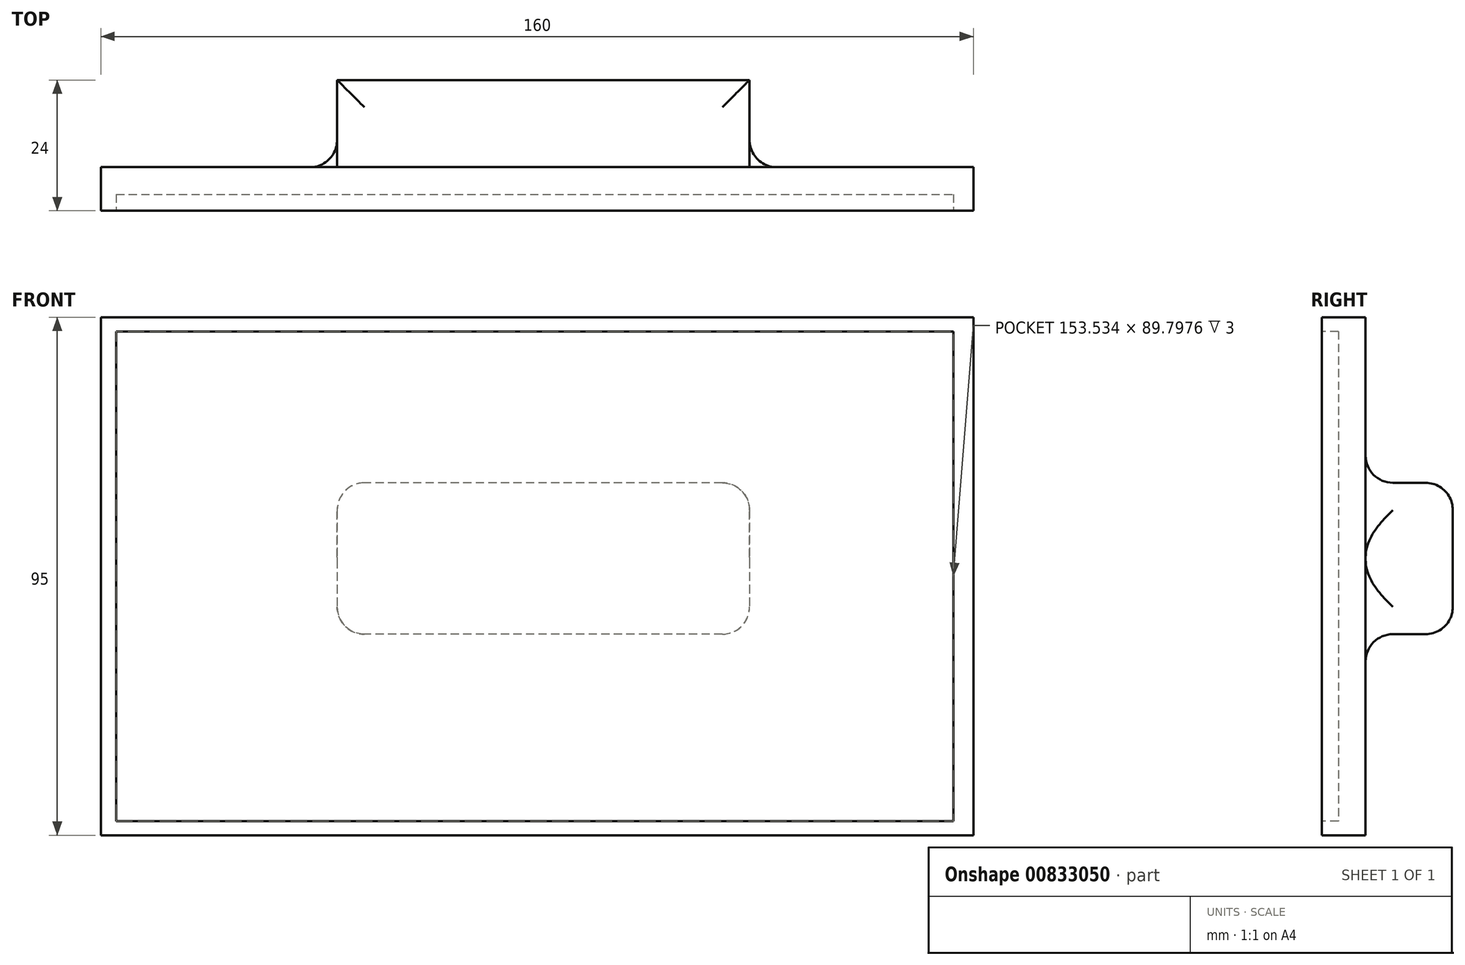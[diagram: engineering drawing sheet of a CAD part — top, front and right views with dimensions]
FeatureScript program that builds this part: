
annotation { "Feature Type Name" : "Feature", "Feature Type Description" : "" }
export const myFeature = defineFeature(function(context is Context, id is Id, definition is map)
    precondition{}
    {
        {
            var Q0;
            Q0=qCreatedBy(makeId("Front.planeOp"),FACE);
            var sketch = newSketch(context, id + "F0", { "sketchPlane" : qUnion([Q0])});
            skLineSegment(sketch, "E0.bottom", {"start": v(-75.9, 65.64) * mm, "end": v(84.1, 65.64) * mm});
            skLineSegment(sketch, "E0.top", {"start": v(-75.9, -29.36) * mm, "end": v(84.1, -29.36) * mm});
            skLineSegment(sketch, "E0.left", {"start": v(-75.9, 65.64) * mm, "end": v(-75.9, -29.36) * mm});
            skLineSegment(sketch, "E0.right", {"start": v(84.1, 65.64) * mm, "end": v(84.1, -29.36) * mm});
            skSolve(sketch);
        }
        {
            var Q0;
            Q0=makeQuery(id+"F0.imprint","IMPRINT",FACE,{"disambiguationData":[TD([[makeQuery(id+"F0.imprint","IMPRINT",EDGE,{"derivedFrom":sQuery(id+"F0.wireOp",EDGE,"E0.bottom")}),-1.0]])]});
            extrude(context, id + "F1", {"entities" : qUnion([Q0]), "depth" : 8 * mm, "offsetDistance" : 25 * mm});
        }
        {
            var Q0;
            Q0=makeQuery(id+"F1.opExtrude","CAP_FACE",FACE,{"disambiguationData":[OSD([sQuery(id+"F0.wireOp",EDGE,"E0.bottom"),sQuery(id+"F0.wireOp",EDGE,"E0.top"),sQuery(id+"F0.wireOp",EDGE,"E0.left"),sQuery(id+"F0.wireOp",EDGE,"E0.right")])],"isStart":false});
            var sketch = newSketch(context, id + "F2", { "sketchPlane" : qUnion([Q0])});
            skLineSegment(sketch, "E1.bottom", {"start": v(-73.1, 63.03) * mm, "end": v(80.44, 63.03) * mm});
            skLineSegment(sketch, "E1.top", {"start": v(-73.1, -26.77) * mm, "end": v(80.44, -26.77) * mm});
            skLineSegment(sketch, "E1.left", {"start": v(-73.1, 63.03) * mm, "end": v(-73.1, -26.77) * mm});
            skLineSegment(sketch, "E1.right", {"start": v(80.44, 63.03) * mm, "end": v(80.44, -26.77) * mm});
            skSolve(sketch);
        }
        {
            var Q0;
            Q0 = qSketchRegion(id + "F2", true);
            extrude(context, id + "F3", {"entities" : qUnion([Q0]), "operationType" : NewBodyOperationType.REMOVE, "oppositeDirection" : true, "depth" : 3 * mm, "offsetDistance" : 25 * mm});
        }
        {
            var Q0;
            Q0=makeQuery(id+"F1.opExtrude","CAP_FACE",FACE,{"disambiguationData":[OSD([sQuery(id+"F0.wireOp",EDGE,"E0.bottom"),sQuery(id+"F0.wireOp",EDGE,"E0.top"),sQuery(id+"F0.wireOp",EDGE,"E0.left"),sQuery(id+"F0.wireOp",EDGE,"E0.right")])],"isStart":true});
            var sketch = newSketch(context, id + "F4", { "sketchPlane" : qUnion([Q0])});
            skLineSegment(sketch, "E2.bottom", {"start": v(-43.05, 35.27) * mm, "end": v(32.59, 35.27) * mm});
            skLineSegment(sketch, "E2.top", {"start": v(-43.05, 7.5) * mm, "end": v(32.59, 7.5) * mm});
            skLineSegment(sketch, "E2.left", {"start": v(-43.05, 35.27) * mm, "end": v(-43.05, 7.5) * mm});
            skLineSegment(sketch, "E2.right", {"start": v(32.59, 35.27) * mm, "end": v(32.59, 7.5) * mm});
            skSolve(sketch);
        }
        {
            var Q0;
            Q0 = qSketchRegion(id + "F4", true);
            extrude(context, id + "F5", {"entities" : qUnion([Q0]), "operationType" : NewBodyOperationType.ADD, "depth" : 16 * mm, "offsetDistance" : 25 * mm});
        }
        {
            var Q0;
            Q0=makeQuery(id+"F5.opExtrude","SWEPT_FACE",FACE,{"disambiguationData":[OSD([sQuery(id+"F4.wireOp",EDGE,"E2.bottom")])]});
            var Q1;
            Q1=makeQuery(id+"F5.opExtrude","SWEPT_FACE",FACE,{"disambiguationData":[OSD([sQuery(id+"F4.wireOp",EDGE,"E2.top")])]});
            fillet(context, id + "F6", {"entities" : qUnion([Q0, Q1]), "radius" : 5 * mm, "tangentPropagation" : true, "allowEdgeOverflow" : false});
        }
    });
